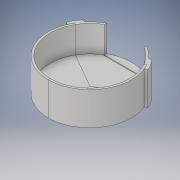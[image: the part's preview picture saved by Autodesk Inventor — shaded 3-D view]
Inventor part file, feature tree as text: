
AUTODESK INVENTOR PART (.ipt)
format: ipt  version: 2019 (Build 230136000, 136)  size: 541,184 bytes
history: native  units: mm
features: sketch x7, extrude x6, plane x5, fillet x4, split x3, loft x2, other x2, boolean_combine x1
ambient origin geometry x8: Origin, YZ Plane, XZ Plane, XY Plane, X Axis, Y Axis, Z Axis, Center Point
bodies: Solid1 (feature_tree), Solid2 (feature_tree), Solid3 (feature_tree), Solid4 (feature_tree), Solid5 (feature_tree), Solid6 (feature_tree), Solid7 (feature_tree)
feature tree (30):
  extrude  "Extrusion1"  Depth=126.0mm
  extrude  "Extrusion2"  Depth=40.0mm
  extrude  "Extrusion3"  Depth=60.0mm
  plane  "Work Plane2"
  plane  "Work Plane3"
  extrude  "Extrusion6"  Depth=10.0mm TaperAngle=0.0deg
  loft  "Loft3"
  extrude  "Extrusion7"  Depth=20.0mm TaperAngle=0.0deg
  loft  "Loft4"
  fillet  "Fillet5"  [1 undecoded]
  fillet  "Fillet6"  [1 undecoded]
  fillet  "Fillet7"  [1 undecoded]
  fillet  "Fillet8"  Radius=20.0mm
  plane  "Work Plane6"
  split  "Split1"
  split  "Split2"
  split  "Split3"
  boolean_combine  "Combine1"
  extrude  "Extrusion8"  TaperAngle=0.0deg  [1 undecoded]
  sketch  "Sketch1"  dims[d0=120.0mm d1=126.0mm]
  sketch  "Sketch2"  dims[d2=40.0mm d3=0.0mm d4=1.0mm]
  sketch  "Sketch3"  dims[d5=1.0mm d6=60.0mm]
  sketch  "Sketch11"  dims[d7=120.0mm d8=10.0mm d9=0.0mm]
  sketch  "Sketch12"  dims[d10=10.0mm d11=0.0mm d21=40.0mm]
  sketch  "Sketch13"  dims[d27=20.0mm d28=20.0mm d29=0.0mm]
  other  "Edges3"
  other  "Edges4"
  plane  "Work Plane4"
  plane  "Work Plane5"
  sketch  "Sketch14"  dims[d36=126.0mm d37=126.0mm d43=120.0deg d45=0.0mm d46=90.0deg d47=0.0mm d48=90.0deg d49=20.0mm d50=0.0mm d51=0.0mm d52=90.0deg d53=0.0mm d54=90.0deg d56=4.0mm d57=4.0mm d58=4.0mm d59=4.0mm d60=20.0mm d61=0.0mm]
note: 4 required parameter values undecoded (feature->parameter linkage not recoverable at this tier; creation-order binding heuristic only, values carry confidence <= 0.55)
